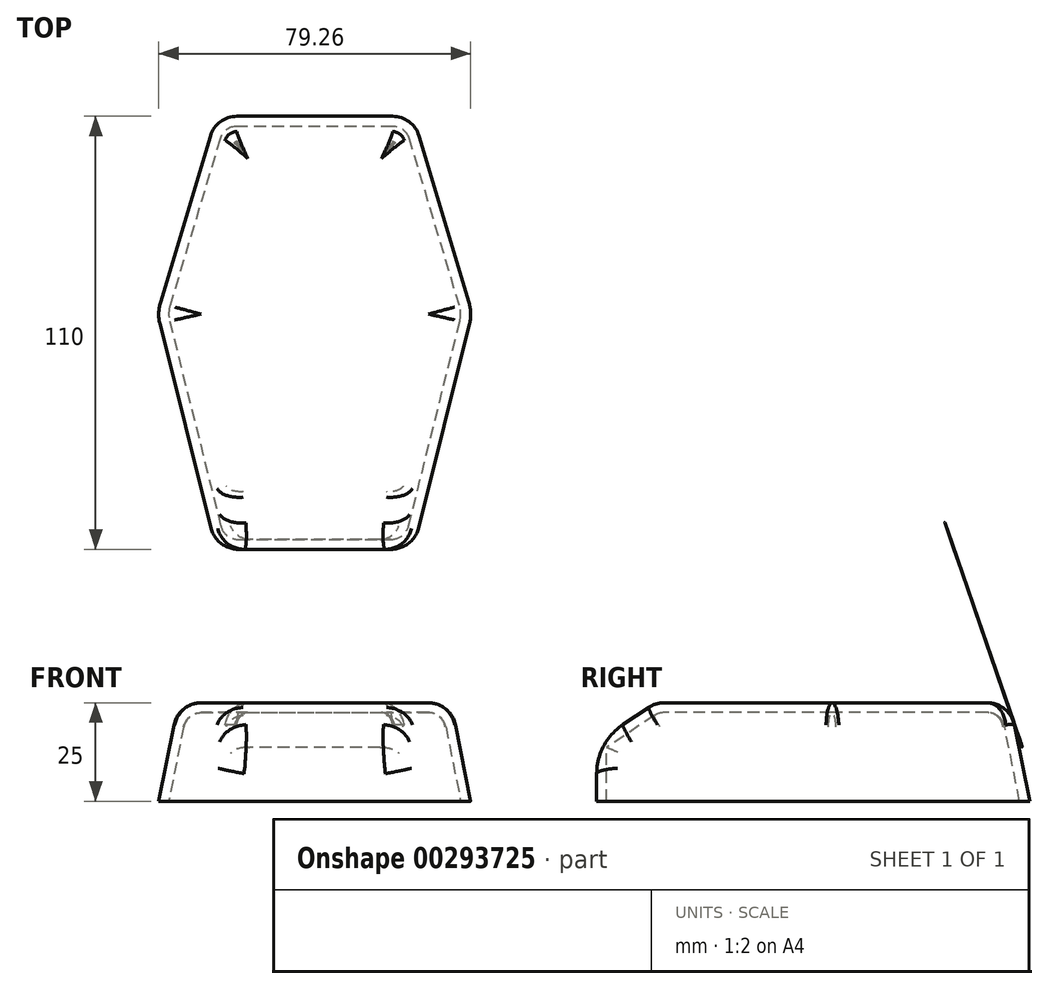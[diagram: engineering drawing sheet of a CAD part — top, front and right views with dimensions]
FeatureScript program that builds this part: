
annotation { "Feature Type Name" : "Feature", "Feature Type Description" : "" }
export const myFeature = defineFeature(function(context is Context, id is Id, definition is map)
    precondition{}
    {
        {
            var Q0;
            Q0=qCreatedBy(makeId("Top.planeOp"),FACE);
            var sketch = newSketch(context, id + "F0", { "sketchPlane" : qUnion([Q0])});
            skLineSegment(sketch, "E0.bottom", {"start": v(-25, 55) * mm, "end": v(25, 55) * mm});
            skLineSegment(sketch, "E0.top", {"start": v(-25, -55) * mm, "end": v(25, -55) * mm});
            skPoint(sketch, "E0.middle", {"position": v(0, 0) * mm});
            skLineSegment(sketch, "E1", {"start": v(-25, 55) * mm, "end": v(-40, 5) * mm});
            skLineSegment(sketch, "E2", {"start": v(-40, 5) * mm, "end": v(-25, -55) * mm});
            skLineSegment(sketch, "E3", {"start": v(25, 55) * mm, "end": v(40, 5) * mm});
            skLineSegment(sketch, "E4", {"start": v(40, 5) * mm, "end": v(25, -55) * mm});
            skPoint(sketch, "E5.orphan", {"position": v(-40, 55) * mm});
            skPoint(sketch, "E6.orphan", {"position": v(-40, -55) * mm});
            skPoint(sketch, "E7.orphan", {"position": v(40, -55) * mm});
            skPoint(sketch, "E8.orphan", {"position": v(40, 55) * mm});
            skSolve(sketch);
        }
        {
            var Q0;
            Q0 = qSketchRegion(id + "F0", true);
            extrude(context, id + "F1", {"entities" : qUnion([Q0]), "depth" : 25 * mm});
        }
        {
            var Q0;
            Q0=makeQuery(id+"F1.opExtrude","SWEPT_EDGE",EDGE,{"disambiguationData":[OSD([sQuery(id+"F0.wireOp",EDGE,"E0.bottom"),sQuery(id+"F0.wireOp",EDGE,"E3")])]});
            fillet(context, id + "F2", {"entities" : qUnion([Q0]), "radius" : 7 * mm, "tangentPropagation" : true, "allowEdgeOverflow" : false});
        }
        {
            var Q0;
            Q0=makeQuery(id+"F1.opExtrude","SWEPT_EDGE",EDGE,{"disambiguationData":[OSD([sQuery(id+"F0.wireOp",EDGE,"E0.bottom"),sQuery(id+"F0.wireOp",EDGE,"E1")])]});
            fillet(context, id + "F3", {"entities" : qUnion([Q0]), "radius" : 7 * mm, "allowEdgeOverflow" : false});
        }
        {
            var Q0;
            Q0=makeQuery(id+"F1.opExtrude","CAP_EDGE",EDGE,{"disambiguationData":[OSD([sQuery(id+"F0.wireOp",EDGE,"E0.top")])],"isStart":false});
            chamfer(context, id + "F4", {"entities" : qUnion([Q0]), "chamferType" : ChamferType.TWO_OFFSETS, "width1" : 15 * mm, "oppositeDirection" : false, "width2" : 10 * mm, "tangentPropagation" : true});
        }
        {
            var Q0;
            Q0=makeQuery(id+"F1.opExtrude","SWEPT_EDGE",EDGE,{"disambiguationData":[OSD([sQuery(id+"F0.wireOp",EDGE,"E1"),sQuery(id+"F0.wireOp",EDGE,"E2")])]});
            var Q1;
            Q1=makeQuery(id+"F1.opExtrude","SWEPT_EDGE",EDGE,{"disambiguationData":[OSD([sQuery(id+"F0.wireOp",EDGE,"E3"),sQuery(id+"F0.wireOp",EDGE,"E4")])]});
            fillet(context, id + "F5", {"entities" : qUnion([Q0, Q1]), "radius" : 10 * mm, "tangentPropagation" : true, "allowEdgeOverflow" : false});
        }
        {
            var Q0;
            Q0=makeQuery(id+"F1.opExtrude","CAP_EDGE",EDGE,{"disambiguationData":[OSD([sQuery(id+"F0.wireOp",EDGE,"E1")])],"isStart":false});
            chamfer(context, id + "F6", {"entities" : qUnion([Q0]), "chamferType" : ChamferType.TWO_OFFSETS, "width1" : 5 * mm, "oppositeDirection" : false, "width2" : 25 * mm, "tangentPropagation" : true});
        }
        {
            var Q0;
            Q0=makeQuery(id+"F6.opChamfer","BLEND_EDGE",EDGE,{"blendedFrom":[makeQuery(id+"F1.opExtrude","CAP_EDGE",EDGE,{"disambiguationData":[OSD([sQuery(id+"F0.wireOp",EDGE,"E2")])],"isStart":false}),makeQuery(id+"F1.opExtrude","SWEPT_FACE",FACE,{"disambiguationData":[OSD([sQuery(id+"F0.wireOp",EDGE,"E0.top")])]})],"blendedInto":[makeQuery(id+"F1.opExtrude","SWEPT_FACE",FACE,{"disambiguationData":[OSD([sQuery(id+"F0.wireOp",EDGE,"E0.top")])]})]});
            var Q1;
            Q1=makeQuery(id+"F6.opChamfer","BLEND_EDGE",EDGE,{"blendedFrom":[makeQuery(id+"F1.opExtrude","CAP_EDGE",EDGE,{"disambiguationData":[OSD([sQuery(id+"F0.wireOp",EDGE,"E2")])],"isStart":false}),makeQuery(id+"F4.opChamfer","BLEND_FACE",FACE,{"disambiguationData":[OSD([sQuery(id+"F0.wireOp",EDGE,"E0.top")])]})],"blendedInto":[makeQuery(id+"F4.opChamfer","BLEND_FACE",FACE,{"disambiguationData":[OSD([sQuery(id+"F0.wireOp",EDGE,"E0.top")])]})]});
            var Q2;
            Q2=makeQuery(id+"F6.opChamfer","BLEND_EDGE",EDGE,{"blendedFrom":[makeQuery(id+"F1.opExtrude","CAP_EDGE",EDGE,{"disambiguationData":[OSD([sQuery(id+"F0.wireOp",EDGE,"E4")])],"isStart":false}),makeQuery(id+"F4.opChamfer","BLEND_FACE",FACE,{"disambiguationData":[OSD([sQuery(id+"F0.wireOp",EDGE,"E0.top")])]})],"blendedInto":[makeQuery(id+"F4.opChamfer","BLEND_FACE",FACE,{"disambiguationData":[OSD([sQuery(id+"F0.wireOp",EDGE,"E0.top")])]})]});
            var Q3;
            Q3=makeQuery(id+"F6.opChamfer","BLEND_EDGE",EDGE,{"blendedFrom":[makeQuery(id+"F1.opExtrude","CAP_EDGE",EDGE,{"disambiguationData":[OSD([sQuery(id+"F0.wireOp",EDGE,"E4")])],"isStart":false}),makeQuery(id+"F1.opExtrude","SWEPT_FACE",FACE,{"disambiguationData":[OSD([sQuery(id+"F0.wireOp",EDGE,"E0.top")])]})],"blendedInto":[makeQuery(id+"F1.opExtrude","SWEPT_FACE",FACE,{"disambiguationData":[OSD([sQuery(id+"F0.wireOp",EDGE,"E0.top")])]})]});
            fillet(context, id + "F7", {"entities" : qUnion([Q0, Q1, Q2, Q3]), "radius" : 7 * mm, "tangentPropagation" : true, "allowEdgeOverflow" : false});
        }
        {
            var Q0;
            {var subQ0=sQuery(id+"F0.wireOp",EDGE,"E2");Q0=makeQuery(id+"F6.opChamfer","BLEND_EDGE",EDGE,{"blendedFrom":[makeQuery(id+"F1.opExtrude","CAP_EDGE",EDGE,{"disambiguationData":[OSD([subQ0])],"isStart":false}),makeQuery(id+"F1.opExtrude","CAP_FACE",FACE,{"disambiguationData":[OSD([sQuery(id+"F0.wireOp",EDGE,"E0.bottom"),sQuery(id+"F0.wireOp",EDGE,"E0.top"),sQuery(id+"F0.wireOp",EDGE,"E1"),subQ0,sQuery(id+"F0.wireOp",EDGE,"E3"),sQuery(id+"F0.wireOp",EDGE,"E4")])],"isStart":false})],"blendedInto":[makeQuery(id+"F1.opExtrude","CAP_FACE",FACE,{"disambiguationData":[OSD([sQuery(id+"F0.wireOp",EDGE,"E0.bottom"),sQuery(id+"F0.wireOp",EDGE,"E0.top"),sQuery(id+"F0.wireOp",EDGE,"E1"),subQ0,sQuery(id+"F0.wireOp",EDGE,"E3"),sQuery(id+"F0.wireOp",EDGE,"E4")])],"isStart":false})]});}
            fillet(context, id + "F8", {"entities" : qUnion([Q0]), "radius" : 7 * mm, "tangentPropagation" : true, "allowEdgeOverflow" : false});
        }
        {
            var Q0;
            Q0=makeQuery(id+"F1.opExtrude","CAP_FACE",FACE,{"disambiguationData":[OSD([sQuery(id+"F0.wireOp",EDGE,"E0.bottom"),sQuery(id+"F0.wireOp",EDGE,"E0.top"),sQuery(id+"F0.wireOp",EDGE,"E1"),sQuery(id+"F0.wireOp",EDGE,"E2"),sQuery(id+"F0.wireOp",EDGE,"E3"),sQuery(id+"F0.wireOp",EDGE,"E4")])],"isStart":true});
            shell(context, id + "F9", {"entities" : qUnion([Q0]), "thickness" : 2.5 * mm});
        }
        {
            var Q0;
            {var subQ0=sQuery(id+"F0.wireOp",EDGE,"E0.top");Q0=makeQuery(id+"F4.opChamfer","BLEND_EDGE",EDGE,{"blendedFrom":[makeQuery(id+"F1.opExtrude","CAP_EDGE",EDGE,{"disambiguationData":[OSD([subQ0])],"isStart":false}),makeQuery(id+"F1.opExtrude","SWEPT_FACE",FACE,{"disambiguationData":[OSD([subQ0])]})],"blendedInto":[makeQuery(id+"F1.opExtrude","SWEPT_FACE",FACE,{"disambiguationData":[OSD([subQ0])]})]});}
            fillet(context, id + "F10", {"entities" : qUnion([Q0]), "radius" : 15 * mm, "tangentPropagation" : true, "allowEdgeOverflow" : false});
        }
    });
